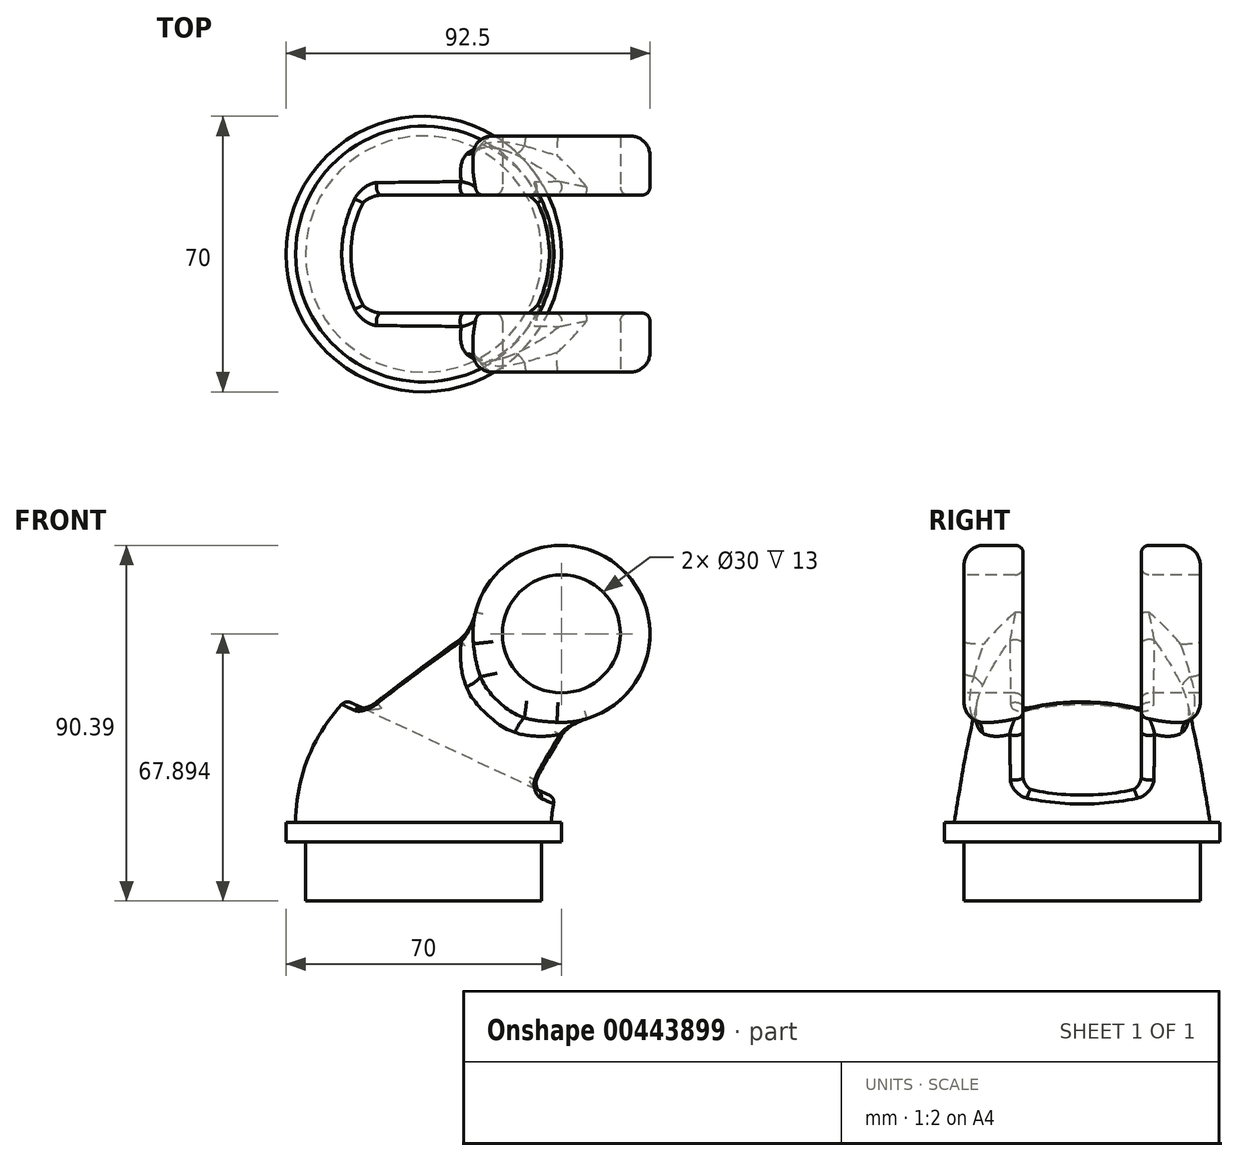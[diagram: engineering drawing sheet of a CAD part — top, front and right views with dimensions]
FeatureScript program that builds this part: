
annotation { "Feature Type Name" : "Feature", "Feature Type Description" : "" }
export const myFeature = defineFeature(function(context is Context, id is Id, definition is map)
    precondition{}
    {
        {
            var Q0;
            Q0=qCreatedBy(makeId("Top.planeOp"),FACE);
            var sketch = newSketch(context, id + "F0", { "sketchPlane" : qUnion([Q0])});
            skCircle(sketch, "E0", {"center": v(0, 0) * mm, "radius": 35 * mm});
            skSolve(sketch);
        }
        {
            var Q0;
            Q0 = qSketchRegion(id + "F0", true);
            extrude(context, id + "F1", {"entities" : qUnion([Q0]), "depth" : 5 * mm});
        }
        {
            var Q0;
            Q0=qCreatedBy(makeId("Front.planeOp"),FACE);
            var sketch = newSketch(context, id + "F2", { "sketchPlane" : qUnion([Q0])});
            skArc(sketch, "E1", {"start": v(17.6, 38.3) * mm, "mid": v(5.55, 23.37) * mm, "end": v(0, 5) * mm});
            skLineSegment(sketch, "E2", {"start": v(17.6, 38.3) * mm, "end": v(35, 52.9) * mm});
            skSolve(sketch);
        }
        {
            var Q0;
            Q0=sQuery(id+"F2.wireOp",EDGE,"E2");
            var Q1;
            Q1=sQuery(id+"F2.wireOp",VERTEX,"E2.end");
            cPlane(context, id + "F3", {"entities" : qUnion([Q0, Q1]), "cplaneType" : CPlaneType.LINE_POINT, "offset" : 25 * mm, "width" : 150 * mm, "height" : 150 * mm});
        }
        {
            var Q0;
            Q0=qCreatedBy(id+"F3.planeOp",FACE);
            var sketch = newSketch(context, id + "F4", { "sketchPlane" : qUnion([Q0])});
            skCircle(sketch, "E3", {"center": v(0, 18.02) * mm, "radius": 22.5 * mm});
            skSolve(sketch);
        }
        {
            var Q0;
            Q0=makeQuery(id+"F1.opExtrude","CAP_FACE",FACE,{"disambiguationData":[OSD([sQuery(id+"F0.wireOp",EDGE,"E0")])],"isStart":false});
            var sketch = newSketch(context, id + "F5", { "sketchPlane" : qUnion([Q0])});
            skCircle(sketch, "E4", {"center": v(0, 0) * mm, "radius": 32.5 * mm});
            skSolve(sketch);
        }
        {
            var Q0;
            Q0=qCreatedBy(makeId("Front.planeOp"),FACE);
            var sketch = newSketch(context, id + "F6", { "sketchPlane" : qUnion([Q0])});
            skArc(sketch, "E5", {"start": v(-16.7, 38.89) * mm, "mid": v(-28.36, 23.7) * mm, "end": v(-32.5, 5) * mm});
            skLineSegment(sketch, "E6", {"start": v(-16.7, 38.89) * mm, "end": v(20.54, 70.13) * mm});
            skSolve(sketch);
        }
        {
            var Q0;
            Q0=qCreatedBy(makeId("Front.planeOp"),FACE);
            var sketch = newSketch(context, id + "F7", { "sketchPlane" : qUnion([Q0])});
            skArc(sketch, "E7", {"start": v(36.35, 17.12) * mm, "mid": v(33.49, 11.36) * mm, "end": v(32.5, 5) * mm});
            skLineSegment(sketch, "E8", {"start": v(36.35, 17.12) * mm, "end": v(49.46, 35.66) * mm});
            skSolve(sketch);
        }
        {
            var Q1;
            Q1=makeQuery(id+"F4.imprint","IMPRINT",FACE,{"disambiguationData":[TD([[makeQuery(id+"F4.imprint","IMPRINT",EDGE,{"derivedFrom":sQuery(id+"F4.wireOp",EDGE,"E3")}),1.0]])]});
            var Q2;
            Q2=makeQuery(id+"F5.imprint","IMPRINT",FACE,{"disambiguationData":[TD([[makeQuery(id+"F5.imprint","IMPRINT",EDGE,{"derivedFrom":sQuery(id+"F5.wireOp",EDGE,"E4")}),1.0]])]});
            var Q3;
            Q3 = qConstructionFilter(qBodyType(qCreatedBy(id + "F6" ,EDGE), BodyType.WIRE), ConstructionObject.NO);
            var Q4;
            Q4 = qConstructionFilter(qBodyType(qCreatedBy(id + "F7" ,EDGE), BodyType.WIRE), ConstructionObject.NO);
            loft(context, id + "F8", {"operationType" : NewBodyOperationType.ADD, "addGuides" : true, "sheetProfilesArray" : [{ "sheetProfileEntities" : qUnion([Q1]) }, { "sheetProfileEntities" : qUnion([Q2]) }], "guidesArray" : [{ "guideEntities" : qUnion([Q3]), "guideDerivativeType" : LoftGuideDerivativeType.DEFAULT, "guideDerivativeMagnitude" : 1 }, { "guideEntities" : qUnion([Q4]), "guideDerivativeType" : LoftGuideDerivativeType.DEFAULT, "guideDerivativeMagnitude" : 1 }]});
        }
        {
            var Q0;
            Q0=qCreatedBy(makeId("Front.planeOp"),FACE);
            var sketch = newSketch(context, id + "F9", { "sketchPlane" : qUnion([Q0])});
            skCircle(sketch, "E9", {"center": v(35, 52.9) * mm, "radius": 22.5 * mm});
            skSolve(sketch);
        }
        {
            var Q0;
            Q0=makeQuery(id+"F9.imprint","IMPRINT",FACE,{"disambiguationData":[TD([[makeQuery(id+"F9.imprint","IMPRINT",EDGE,{"derivedFrom":sQuery(id+"F9.wireOp",EDGE,"E9")}),1.0]])]});
            extrude(context, id + "F10", {"entities" : qUnion([Q0]), "operationType" : NewBodyOperationType.ADD, "endBound" : BoundingType.SYMMETRIC, "depth" : 60 * mm});
        }
        {
            var Q0;
            Q0=makeQuery(id+"F10.boolean.opBoolean","INTERSECT",EDGE,{"derivedFrom":[makeQuery(id+"F8.opLoft","SWEPT_FACE",FACE,{"disambiguationData":[OSD([sQuery(id+"F4.wireOp",EDGE,"E3"),sQuery(id+"F5.wireOp",EDGE,"E4"),sQuery(id+"F6.wireOp",VERTEX,"E6.start"),sQuery(id+"F6.wireOp",EDGE,"E5"),sQuery(id+"F6.wireOp",EDGE,"E6"),sQuery(id+"F7.wireOp",VERTEX,"E8.start"),sQuery(id+"F7.wireOp",EDGE,"E7"),sQuery(id+"F7.wireOp",EDGE,"E8")])]}),makeQuery(id+"F10.opExtrude","SWEPT_FACE",FACE,{"disambiguationData":[OSD([sQuery(id+"F9.wireOp",EDGE,"E9")])]})]});
            fillet(context, id + "F11", {"entities" : qUnion([Q0]), "radius" : 5 * mm, "tangentPropagation" : true, "allowEdgeOverflow" : false});
        }
        {
            var Q0;
            Q0=makeQuery(id+"F10.opExtrude","CAP_EDGE",EDGE,{"disambiguationData":[OSD([sQuery(id+"F9.wireOp",EDGE,"E9")])],"isStart":true});
            var Q1;
            Q1=makeQuery(id+"F10.opExtrude","CAP_EDGE",EDGE,{"disambiguationData":[OSD([sQuery(id+"F9.wireOp",EDGE,"E9")])],"isStart":false});
            fillet(context, id + "F12", {"entities" : qUnion([Q0, Q1]), "radius" : 5 * mm, "tangentPropagation" : true, "allowEdgeOverflow" : false});
        }
        {
            var Q0;
            Q0=makeQuery(id+"F10.opExtrude","CAP_FACE",FACE,{"disambiguationData":[OSD([sQuery(id+"F9.wireOp",EDGE,"E9")])],"isStart":false});
            var sketch = newSketch(context, id + "F13", { "sketchPlane" : qUnion([Q0])});
            skCircle(sketch, "E10", {"center": v(35, 52.9) * mm, "radius": 15 * mm});
            skSolve(sketch);
        }
        {
            var Q0;
            Q0 = qSketchRegion(id + "F13", true);
            extrude(context, id + "F14", {"entities" : qUnion([Q0]), "operationType" : NewBodyOperationType.REMOVE, "endBound" : BoundingType.THROUGH_ALL, "oppositeDirection" : true, "depth" : 25 * mm});
        }
        {
            var Q0;
            Q0=qCreatedBy(makeId("Front.planeOp"),FACE);
            var sketch = newSketch(context, id + "F15", { "sketchPlane" : qUnion([Q0])});
            skLineSegment(sketch, "E11", {"start": v(-104.18, 75.4) * mm, "end": v(57.5, 0) * mm});
            skLineSegment(sketch, "E12", {"start": v(57.5, 75.4) * mm, "end": v(57.5, 0) * mm});
            skLineSegment(sketch, "E13", {"start": v(-104.18, 75.4) * mm, "end": v(57.5, 75.4) * mm});
            skSolve(sketch);
        }
        {
            var Q0;
            Q0=makeQuery(id+"F15.imprint","IMPRINT",FACE,{"disambiguationData":[TD([[makeQuery(id+"F15.imprint","IMPRINT",EDGE,{"derivedFrom":sQuery(id+"F15.wireOp",EDGE,"E11")}),1.0]])]});
            extrude(context, id + "F16", {"entities" : qUnion([Q0]), "operationType" : NewBodyOperationType.REMOVE, "endBound" : BoundingType.SYMMETRIC, "oppositeDirection" : true, "depth" : 30 * mm});
        }
        {
            var Q0;
            Q0=qCreatedBy(makeId("Front.planeOp"),FACE);
            var sketch = newSketch(context, id + "F17", { "sketchPlane" : qUnion([Q0])});
            skLineSegment(sketch, "E14.bottom", {"start": v(0, 0) * mm, "end": v(-30, 0) * mm});
            skLineSegment(sketch, "E14.top", {"start": v(0, -15) * mm, "end": v(-30, -15) * mm});
            skLineSegment(sketch, "E14.left", {"start": v(0, 0) * mm, "end": v(0, -15) * mm});
            skLineSegment(sketch, "E14.right", {"start": v(-30, 0) * mm, "end": v(-30, -15) * mm});
            skSolve(sketch);
        }
        {
            var Q0;
            Q0=makeQuery(id+"F17.imprint","IMPRINT",FACE,{"disambiguationData":[TD([[makeQuery(id+"F17.imprint","IMPRINT",EDGE,{"derivedFrom":sQuery(id+"F17.wireOp",EDGE,"E14.bottom")}),1.0]])]});
            var Q1;
            Q1=sQuery(id+"F17.wireOp",EDGE,"E14.left");
            revolve(context, id + "F18", {"operationType" : NewBodyOperationType.ADD, "entities" : qUnion([Q0]), "axis" : qUnion([Q1]), "revolveType" : RevolveType.FULL});
        }
        {
            var Q0;
            Q0=makeQuery(id+"F16.boolean.opBoolean","INTERSECT",EDGE,{"derivedFrom":[makeQuery(id+"F14.boolean.opBoolean","COPY",FACE,{"derivedFrom":makeQuery(id+"F14.opExtrude","SWEPT_FACE",FACE,{"disambiguationData":[OSD([sQuery(id+"F13.wireOp",EDGE,"E10")])]})}),makeQuery(id+"F16.opExtrude","CAP_FACE",FACE,{"disambiguationData":[OSD([sQuery(id+"F15.wireOp",EDGE,"E11"),sQuery(id+"F15.wireOp",EDGE,"E12"),sQuery(id+"F15.wireOp",EDGE,"E13")])],"isStart":true})]});
            var Q1;
            Q1=makeQuery(id+"F16.boolean.opBoolean","COPY",FACE,{"derivedFrom":makeQuery(id+"F16.opExtrude","SWEPT_FACE",FACE,{"disambiguationData":[OSD([sQuery(id+"F15.wireOp",EDGE,"E11")])]})});
            var Q2;
            Q2=makeQuery(id+"F16.boolean.opBoolean","COPY",FACE,{"derivedFrom":makeQuery(id+"F16.opExtrude","CAP_FACE",FACE,{"disambiguationData":[OSD([sQuery(id+"F15.wireOp",EDGE,"E11"),sQuery(id+"F15.wireOp",EDGE,"E12"),sQuery(id+"F15.wireOp",EDGE,"E13")])],"isStart":true})});
            var Q3;
            Q3=makeQuery(id+"F16.boolean.opBoolean","INTERSECT",EDGE,{"derivedFrom":[makeQuery(id+"F14.boolean.opBoolean","COPY",FACE,{"derivedFrom":makeQuery(id+"F14.opExtrude","SWEPT_FACE",FACE,{"disambiguationData":[OSD([sQuery(id+"F13.wireOp",EDGE,"E10")])]})}),makeQuery(id+"F16.opExtrude","CAP_FACE",FACE,{"disambiguationData":[OSD([sQuery(id+"F15.wireOp",EDGE,"E11"),sQuery(id+"F15.wireOp",EDGE,"E12"),sQuery(id+"F15.wireOp",EDGE,"E13")])],"isStart":false})]});
            var Q4;
            Q4=makeQuery(id+"F16.boolean.opBoolean","COPY",FACE,{"derivedFrom":makeQuery(id+"F16.opExtrude","CAP_FACE",FACE,{"disambiguationData":[OSD([sQuery(id+"F15.wireOp",EDGE,"E11"),sQuery(id+"F15.wireOp",EDGE,"E12"),sQuery(id+"F15.wireOp",EDGE,"E13")])],"isStart":false})});
            fillet(context, id + "F19", {"entities" : qUnion([Q0, Q1, Q2, Q3, Q4]), "radius" : 2 * mm, "tangentPropagation" : true, "allowEdgeOverflow" : false});
        }
    });
